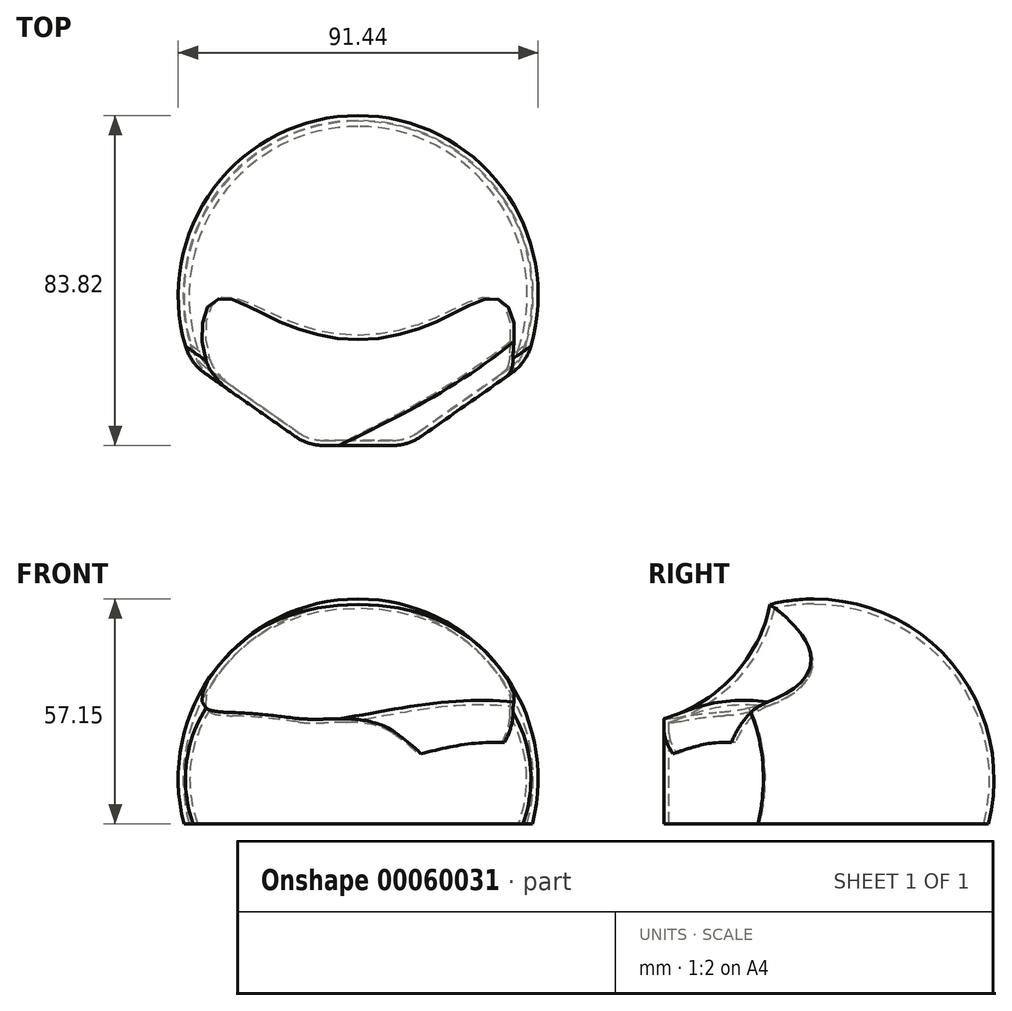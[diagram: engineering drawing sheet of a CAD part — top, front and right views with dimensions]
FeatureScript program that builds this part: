
annotation { "Feature Type Name" : "Feature", "Feature Type Description" : "" }
export const myFeature = defineFeature(function(context is Context, id is Id, definition is map)
    precondition{}
    {
        {
            var Q0;
            Q0=qCreatedBy(makeId("Right.planeOp"),FACE);
            var sketch = newSketch(context, id + "F0", { "sketchPlane" : qUnion([Q0])});
            skLineSegment(sketch, "E0", {"start": v(0, -34.3) * mm, "end": v(0, 57.15) * mm, "construction": true});
            skArc(sketch, "E1", {"start": v(0, -34.3) * mm, "mid": v(45.72, 11.43) * mm, "end": v(0, 57.15) * mm, "construction": true});
            skLineSegment(sketch, "E2", {"start": v(0, 0) * mm, "end": v(0, 57.15) * mm});
            skArc(sketch, "E3", {"start": v(44.27, 0) * mm, "mid": v(36.14, 39.43) * mm, "end": v(0, 57.15) * mm});
            skLineSegment(sketch, "E4", {"start": v(0, 0) * mm, "end": v(44.27, 0) * mm});
            skSolve(sketch);
        }
        {
            var Q0;
            Q0 = qSketchRegion(id + "F0", true);
            var Q1;
            Q1=sQuery(id+"F0.wireOp",EDGE,"E2");
            revolve(context, id + "F1", {"entities" : qUnion([Q0]), "axis" : qUnion([Q1]), "revolveType" : RevolveType.FULL});
        }
        {
            var Q0;
            Q0=qCreatedBy(makeId("Top.planeOp"),FACE);
            var sketch = newSketch(context, id + "F2", { "sketchPlane" : qUnion([Q0])});
            skLineSegment(sketch, "E5", {"start": v(-12.7, -38.1) * mm, "end": v(12.7, -38.1) * mm});
            skLineSegment(sketch, "E6", {"start": v(0, 0) * mm, "end": v(0, -38.1) * mm, "construction": true});
            skLineSegment(sketch, "E7", {"start": v(12.7, -38.1) * mm, "end": v(54.18, -9.05) * mm});
            skLineSegment(sketch, "E8", {"start": v(54.18, -9.05) * mm, "end": v(54.18, -79.9) * mm});
            skLineSegment(sketch, "E9", {"start": v(54.18, -79.9) * mm, "end": v(-54.18, -79.9) * mm});
            skLineSegment(sketch, "E10", {"start": v(-54.18, -79.9) * mm, "end": v(-54.18, -9.05) * mm});
            skLineSegment(sketch, "E11", {"start": v(-54.18, -9.05) * mm, "end": v(-12.7, -38.1) * mm});
            skLineSegment(sketch, "E12", {"start": v(54.18, -9.05) * mm, "end": v(-54.18, -9.05) * mm, "construction": true});
            skPoint(sketch, "E13", {"position": v(0, -9.05) * mm});
            skSolve(sketch);
        }
        {
            var Q0;
            Q0 = qSketchRegion(id + "F2", true);
            extrude(context, id + "F3", {"entities" : qUnion([Q0]), "operationType" : NewBodyOperationType.REMOVE, "endBound" : BoundingType.THROUGH_ALL, "depth" : 25.4 * mm});
        }
        {
            var Q0;
            Q0=qCreatedBy(makeId("Right.planeOp"),FACE);
            var sketch = newSketch(context, id + "F4", { "sketchPlane" : qUnion([Q0])});
            skArc(sketch, "E14", {"start": v(-46.97, 25.4) * mm, "mid": v(-24.58, 37.92) * mm, "end": v(-7.62, 57.15) * mm});
            skLineSegment(sketch, "E15", {"start": v(0, 57.15) * mm, "end": v(-7.62, 57.15) * mm, "construction": true});
            skLineSegment(sketch, "E16", {"start": v(-7.62, 57.15) * mm, "end": v(-46.97, 71.5) * mm});
            skLineSegment(sketch, "E17", {"start": v(-46.97, 71.5) * mm, "end": v(-46.97, 25.4) * mm});
            skSolve(sketch);
        }
        {
            var Q0;
            Q0=qCreatedBy(makeId("Top.planeOp"),FACE);
            var Q1;
            Q1=sQuery(id+"F4.wireOp",VERTEX,"E15.start");
            cPlane(context, id + "F5", {"entities" : qUnion([Q0, Q1]), "cplaneType" : CPlaneType.PLANE_POINT, "offset" : 152.4 * mm, "width" : 152.4 * mm, "height" : 152.4 * mm});
        }
        {
            var Q0;
            Q0=qCreatedBy(id+"F5.planeOp",FACE);
            var sketch = newSketch(context, id + "F6", { "sketchPlane" : qUnion([Q0])});
            skArc(sketch, "E18", {"start": v(-63.5, 14.05) * mm, "mid": v(0, -38.1) * mm, "end": v(63.5, 14.05) * mm});
            skLineSegment(sketch, "E19", {"start": v(-63.5, 14.05) * mm, "end": v(63.5, 14.05) * mm, "construction": true});
            skPoint(sketch, "E20", {"position": v(0, -38.1) * mm});
            skSolve(sketch);
        }
        {
            var Q0;
            Q0=qCreatedBy(makeId("Right.planeOp"),FACE);
            var sketch = newSketch(context, id + "F7", { "sketchPlane" : qUnion([Q0])});
            skArc(sketch, "E21", {"start": v(-50.8, 25.4) * mm, "mid": v(-24.77, 33.62) * mm, "end": v(-10.92, 57.15) * mm});
            skLineSegment(sketch, "E22", {"start": v(-50.8, 25.4) * mm, "end": v(-45.1, 64.9) * mm});
            skLineSegment(sketch, "E23", {"start": v(-45.1, 64.9) * mm, "end": v(-10.92, 57.15) * mm});
            skSolve(sketch);
        }
        {
            var Q0;
            Q0=makeQuery(id+"F7.imprint","IMPRINT",FACE,{"disambiguationData":[TD([[makeQuery(id+"F7.imprint","IMPRINT",EDGE,{"derivedFrom":sQuery(id+"F7.wireOp",EDGE,"E21")}),1.0]])]});
            var Q1;
            Q1=sQuery(id+"F6.wireOp",EDGE,"E18");
            sweep(context, id + "F8", {"operationType" : NewBodyOperationType.REMOVE, "profiles" : qUnion([Q0]), "path" : qUnion([Q1])});
        }
        {
            var Q0;
            Q0=makeQuery(id+"F1.opRevolve","SWEPT_BODY",BODY,{"disambiguationData":[OSD([sQuery(id+"F0.wireOp",EDGE,"E2"),sQuery(id+"F0.wireOp",EDGE,"E3"),sQuery(id+"F0.wireOp",EDGE,"E4")])]});
            var Q1;
            Q1=qCreatedBy(makeId("Right.planeOp"),FACE);
            mirror(context, id + "F9", {"operationType" : NewBodyOperationType.INTERSECT, "entities" : qUnion([Q0]), "mirrorPlane" : qUnion([Q1])});
        }
        {
            var Q0;
            {var subQ0=makeQuery(id+"F1.opRevolve","SWEPT_FACE",FACE,{"disambiguationData":[OSD([sQuery(id+"F0.wireOp",EDGE,"E3")])]});Q0=makeQuery(id+"F9.boolean.opBoolean","INTERSECT",EDGE,{"derivedFrom":[subQ0,makeQuery(id+"F9.boolean.toolComplement.opBoolean","COPY",FACE,{"derivedFrom":makeQuery(id+"F9.opPattern","COPY",FACE,{"derivedFrom":subQ0,"instanceName":"1"})})]});}
            var Q1;
            Q1=makeQuery(id+"F3.boolean.opBoolean","INTERSECT",EDGE,{"derivedFrom":[makeQuery(id+"F1.opRevolve","SWEPT_FACE",FACE,{"disambiguationData":[OSD([sQuery(id+"F0.wireOp",EDGE,"E3")])]}),makeQuery(id+"F3.opExtrude","SWEPT_FACE",FACE,{"disambiguationData":[OSD([sQuery(id+"F2.wireOp",EDGE,"E7")])]})]});
            var Q2;
            Q2=makeQuery(id+"F3.boolean.opBoolean","INTERSECT",EDGE,{"derivedFrom":[makeQuery(id+"F1.opRevolve","SWEPT_FACE",FACE,{"disambiguationData":[OSD([sQuery(id+"F0.wireOp",EDGE,"E3")])]}),makeQuery(id+"F3.opExtrude","SWEPT_FACE",FACE,{"disambiguationData":[OSD([sQuery(id+"F2.wireOp",EDGE,"E11")])]})]});
            var Q3;
            Q3=makeQuery(id+"F8.boolean.opBoolean","INTERSECT",EDGE,{"derivedFrom":[makeQuery(id+"F3.boolean.opBoolean","COPY",FACE,{"derivedFrom":makeQuery(id+"F3.opExtrude","SWEPT_FACE",FACE,{"disambiguationData":[OSD([sQuery(id+"F2.wireOp",EDGE,"E7")])]})}),makeQuery(id+"F8.opSweep","SWEPT_FACE",FACE,{"disambiguationData":[OSD([sQuery(id+"F6.wireOp",EDGE,"E18"),sQuery(id+"F7.wireOp",EDGE,"E21")])]})]});
            var Q4;
            {var subQ0=makeQuery(id+"F3.boolean.opBoolean","COPY",FACE,{"derivedFrom":makeQuery(id+"F3.opExtrude","SWEPT_FACE",FACE,{"disambiguationData":[OSD([sQuery(id+"F2.wireOp",EDGE,"E5")])]})});Q4=makeQuery(id+"F9.boolean.opBoolean","INTERSECT",EDGE,{"derivedFrom":[subQ0,makeQuery(id+"F9.boolean.toolComplement.opBoolean","COPY",FACE,{"derivedFrom":makeQuery(id+"F9.opPattern","COPY",FACE,{"derivedFrom":subQ0,"instanceName":"1"})})]});}
            var Q5;
            Q5=makeQuery(id+"F9.boolean.opBoolean","COPY",EDGE,{"derivedFrom":makeQuery(id+"F9.boolean.toolComplement.opBoolean","COPY",EDGE,{"derivedFrom":makeQuery(id+"F9.opPattern","COPY",EDGE,{"derivedFrom":makeQuery(id+"F8.boolean.opBoolean","INTERSECT",EDGE,{"derivedFrom":[makeQuery(id+"F3.boolean.opBoolean","COPY",FACE,{"derivedFrom":makeQuery(id+"F3.opExtrude","SWEPT_FACE",FACE,{"disambiguationData":[OSD([sQuery(id+"F2.wireOp",EDGE,"E7")])]})}),makeQuery(id+"F8.opSweep","SWEPT_FACE",FACE,{"disambiguationData":[OSD([sQuery(id+"F6.wireOp",EDGE,"E18"),sQuery(id+"F7.wireOp",EDGE,"E21")])]})]}),"instanceName":"1"})})});
            var Q6;
            Q6=makeQuery(id+"F3.boolean.opBoolean","COPY",EDGE,{"derivedFrom":makeQuery(id+"F3.opExtrude","SWEPT_EDGE",EDGE,{"disambiguationData":[OSD([sQuery(id+"F2.wireOp",EDGE,"E5"),sQuery(id+"F2.wireOp",EDGE,"E7")])]})});
            var Q7;
            Q7=makeQuery(id+"F3.boolean.opBoolean","COPY",EDGE,{"derivedFrom":makeQuery(id+"F3.opExtrude","SWEPT_EDGE",EDGE,{"disambiguationData":[OSD([sQuery(id+"F2.wireOp",EDGE,"E5"),sQuery(id+"F2.wireOp",EDGE,"E11")])]})});
            fillet(context, id + "F10", {"entities" : qUnion([Q0, Q1, Q2, Q3, Q4, Q5, Q6, Q7]), "radius" : 12.7 * mm, "tangentPropagation" : true, "allowEdgeOverflow" : false});
        }
        {
            var Q0;
            Q0=makeQuery(id+"F1.opRevolve","SWEPT_FACE",FACE,{"disambiguationData":[OSD([sQuery(id+"F0.wireOp",EDGE,"E4")])]});
            shell(context, id + "F11", {"entities" : qUnion([Q0]), "thickness" : 1.27 * mm});
        }
    });
